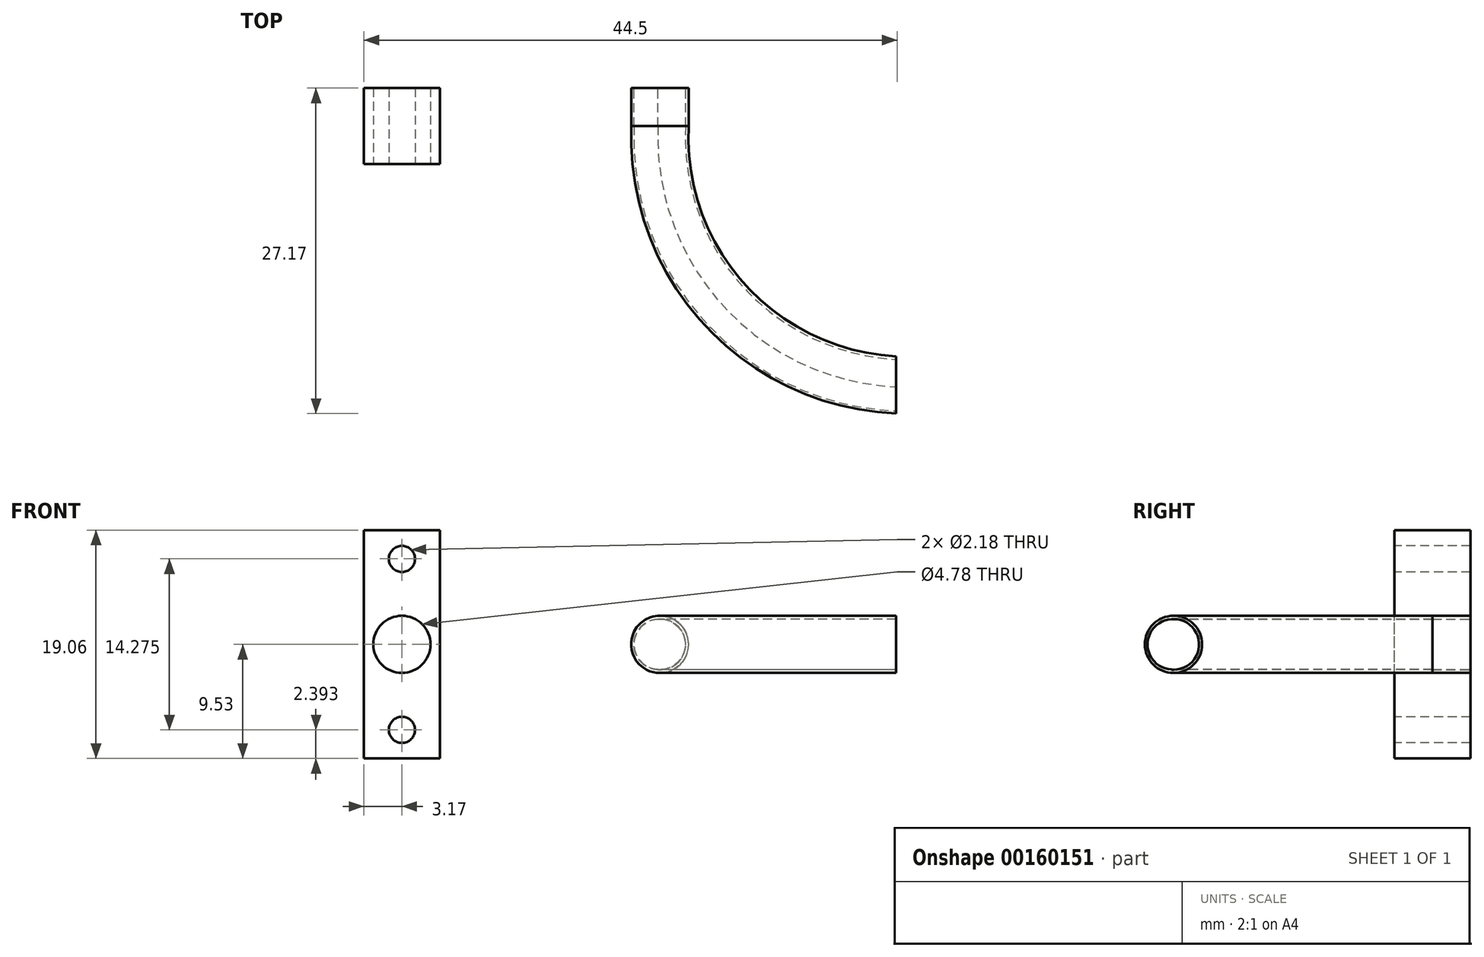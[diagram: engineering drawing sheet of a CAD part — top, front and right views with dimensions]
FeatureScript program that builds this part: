
annotation { "Feature Type Name" : "Feature", "Feature Type Description" : "" }
export const myFeature = defineFeature(function(context is Context, id is Id, definition is map)
    precondition{}
    {
        {
            var Q0;
            Q0=qCreatedBy(makeId("Front.planeOp"),FACE);
            var sketch = newSketch(context, id + "F0", { "sketchPlane" : qUnion([Q0])});
            skLineSegment(sketch, "E0.bottom", {"start": v(3.17, -9.53) * mm, "end": v(-3.18, -9.53) * mm});
            skLineSegment(sketch, "E0.top", {"start": v(3.18, 9.53) * mm, "end": v(-3.17, 9.53) * mm});
            skLineSegment(sketch, "E0.left", {"start": v(3.17, -9.53) * mm, "end": v(3.18, 9.53) * mm});
            skLineSegment(sketch, "E0.right", {"start": v(-3.18, -9.53) * mm, "end": v(-3.17, 9.53) * mm});
            skPoint(sketch, "E0.middle", {"position": v(0, 0) * mm});
            skSolve(sketch);
        }
        {
            var Q0;
            Q0 = qSketchRegion(id + "F0", true);
            extrude(context, id + "F1", {"entities" : qUnion([Q0]), "depth" : 6.35 * mm});
        }
        {
            var Q0;
            Q0=makeQuery(id+"F1.opExtrude","CAP_FACE",FACE,{"disambiguationData":[OSD([sQuery(id+"F0.wireOp",EDGE,"E0.bottom"),sQuery(id+"F0.wireOp",EDGE,"E0.top"),sQuery(id+"F0.wireOp",EDGE,"E0.left"),sQuery(id+"F0.wireOp",EDGE,"E0.right")])],"isStart":false});
            var sketch = newSketch(context, id + "F2", { "sketchPlane" : qUnion([Q0])});
            skLineSegment(sketch, "E1", {"start": v(-12.79, 0) * mm, "end": v(15.93, 0) * mm, "construction": true});
            skLineSegment(sketch, "E2", {"start": v(0, 12.62) * mm, "end": v(0, -14.67) * mm, "construction": true});
            skPoint(sketch, "E2.startSnap0", {"position": v(0, 9.53) * mm});
            skLineSegment(sketch, "E3", {"start": v(-9.09, 7.14) * mm, "end": v(9.3, 7.14) * mm, "construction": true});
            skLineSegment(sketch, "E4", {"start": v(-10.8, -7.14) * mm, "end": v(16.02, -7.14) * mm, "construction": true});
            skCircle(sketch, "E5", {"center": v(0, 7.14) * mm, "radius": 1.1 * mm});
            skCircle(sketch, "E6", {"center": v(0, -7.14) * mm, "radius": 1.1 * mm});
            skSolve(sketch);
        }
        {
            var Q0;
            Q0 = qSketchRegion(id + "F2", true);
            extrude(context, id + "F3", {"entities" : qUnion([Q0]), "operationType" : NewBodyOperationType.REMOVE, "endBound" : BoundingType.THROUGH_ALL, "oppositeDirection" : true, "depth" : 25.4 * mm});
        }
        {
            var Q0;
            Q0=makeQuery(id+"F1.opExtrude","CAP_FACE",FACE,{"disambiguationData":[OSD([sQuery(id+"F0.wireOp",EDGE,"E0.bottom"),sQuery(id+"F0.wireOp",EDGE,"E0.top"),sQuery(id+"F0.wireOp",EDGE,"E0.left"),sQuery(id+"F0.wireOp",EDGE,"E0.right")])],"isStart":false});
            var sketch = newSketch(context, id + "F4", { "sketchPlane" : qUnion([Q0])});
            skCircle(sketch, "E7", {"center": v(0, 0) * mm, "radius": 2.39 * mm});
            skSolve(sketch);
        }
        {
            var Q0;
            Q0 = qSketchRegion(id + "F4", true);
            extrude(context, id + "F5", {"entities" : qUnion([Q0]), "operationType" : NewBodyOperationType.REMOVE, "endBound" : BoundingType.THROUGH_ALL, "oppositeDirection" : true, "depth" : 25.4 * mm});
        }
        {
            var Q0;
            Q0=qCreatedBy(makeId("Front.planeOp"),FACE);
            var sketch = newSketch(context, id + "F6", { "sketchPlane" : qUnion([Q0])});
            skLineSegment(sketch, "E8", {"start": v(0, 0) * mm, "end": v(21.54, 0) * mm, "construction": true});
            skCircle(sketch, "E9", {"center": v(21.54, 0) * mm, "radius": 2.39 * mm});
            skSolve(sketch);
        }
        {
            var Q0;
            Q0 = qSketchRegion(id + "F6", true);
            extrude(context, id + "F7", {"entities" : qUnion([Q0]), "depth" : 3.17 * mm});
        }
        {
            var Q0;
            Q0=qCreatedBy(makeId("Front.planeOp"),FACE);
            var sketch = newSketch(context, id + "F8", { "sketchPlane" : qUnion([Q0])});
            skLineSegment(sketch, "E10", {"start": v(21.47, 0) * mm, "end": v(21.47, 2.39) * mm, "construction": true});
            skCircle(sketch, "E11", {"center": v(21.47, 0) * mm, "radius": 2.1 * mm});
            skSolve(sketch);
        }
        {
            var Q0;
            Q0 = qSketchRegion(id + "F8", true);
            extrude(context, id + "F9", {"entities" : qUnion([Q0]), "operationType" : NewBodyOperationType.REMOVE, "endBound" : BoundingType.THROUGH_ALL, "depth" : 25.4 * mm});
        }
        {
            var Q0;
            Q0=qCreatedBy(makeId("Front.planeOp"),FACE);
            var sketch = newSketch(context, id + "F10", { "sketchPlane" : qUnion([Q0])});
            skLineSegment(sketch, "E12", {"start": v(21.56, 2.37) * mm, "end": v(21.56, 0) * mm, "construction": true});
            skCircle(sketch, "E13", {"center": v(21.56, 0) * mm, "radius": 2.11 * mm});
            skSolve(sketch);
        }
        {
            var Q0;
            Q0 = qSketchRegion(id + "F10", true);
            extrude(context, id + "F11", {"entities" : qUnion([Q0]), "operationType" : NewBodyOperationType.REMOVE, "endBound" : BoundingType.THROUGH_ALL, "depth" : 25.4 * mm});
        }
        {
            var Q0;
            Q0=qCreatedBy(makeId("Top.planeOp"),FACE);
            var sketch = newSketch(context, id + "F12", { "sketchPlane" : qUnion([Q0])});
            skArc(sketch, "E14", {"start": v(21.7, -4.13) * mm, "mid": v(27.7, -18.63) * mm, "end": v(42.2, -24.63) * mm});
            skSolve(sketch);
        }
        {
            var Q0;
            Q0=makeQuery(id+"F7.opExtrude","CAP_FACE",FACE,{"disambiguationData":[OSD([sQuery(id+"F6.wireOp",EDGE,"E9")])],"isStart":false});
            var Q1;
            Q1=sQuery(id+"F12.wireOp",EDGE,"E14");
            sweep(context, id + "F13", {"operationType" : NewBodyOperationType.ADD, "profiles" : qUnion([Q0]), "path" : qUnion([Q1])});
        }
    });
